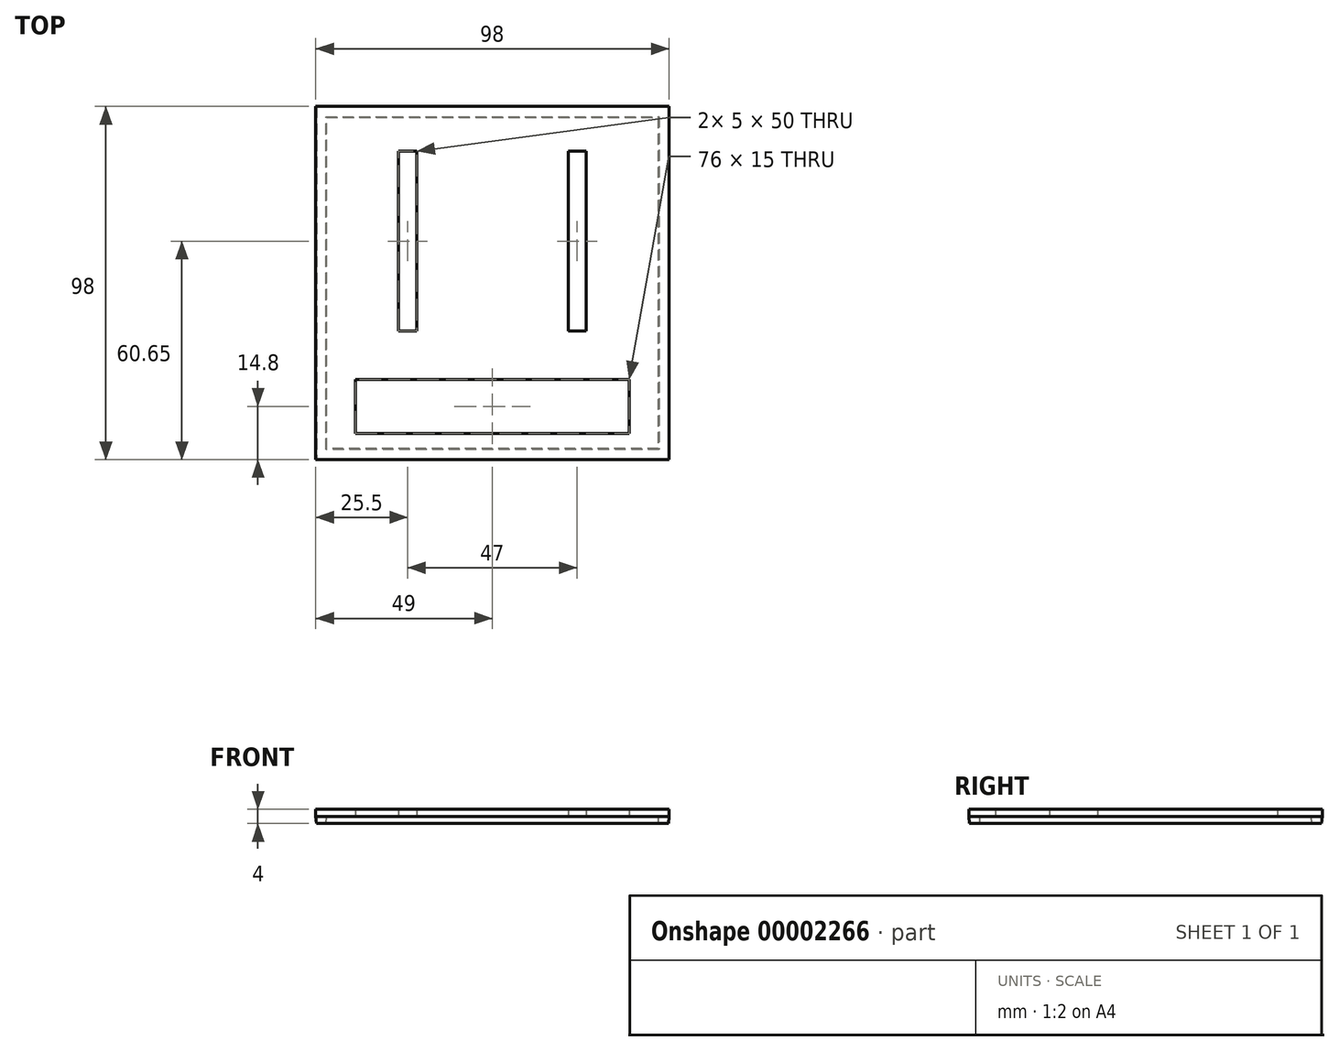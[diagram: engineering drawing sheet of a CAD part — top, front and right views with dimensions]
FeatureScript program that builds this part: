
annotation { "Feature Type Name" : "Feature", "Feature Type Description" : "" }
export const myFeature = defineFeature(function(context is Context, id is Id, definition is map)
    precondition{}
    {
        {
            var Q0;
            Q0=qCreatedBy(makeId("Top.planeOp"),FACE);
            var sketch = newSketch(context, id + "F0", { "sketchPlane" : qUnion([Q0])});
            skLineSegment(sketch, "E0.bottom", {"start": v(46, -46) * mm, "end": v(-46, -46) * mm});
            skLineSegment(sketch, "E0.top", {"start": v(46, 46) * mm, "end": v(-46, 46) * mm});
            skLineSegment(sketch, "E0.left", {"start": v(46, -46) * mm, "end": v(46, 46) * mm});
            skLineSegment(sketch, "E0.right", {"start": v(-46, -46) * mm, "end": v(-46, 46) * mm});
            skPoint(sketch, "E0.middle", {"position": v(0, 0) * mm});
            skLineSegment(sketch, "E1", {"start": v(0, 46) * mm, "end": v(0, -46) * mm, "construction": true});
            skLineSegment(sketch, "E2", {"start": v(0, -41.7) * mm, "end": v(38, -41.7) * mm});
            skLineSegment(sketch, "E3", {"start": v(38, -41.7) * mm, "end": v(38, -26.7) * mm});
            skLineSegment(sketch, "E4", {"start": v(38, -26.7) * mm, "end": v(0, -26.7) * mm});
            skLineSegment(sketch, "E5.bottom", {"start": v(49, 49) * mm, "end": v(-49, 49) * mm});
            skLineSegment(sketch, "E5.top", {"start": v(49, -49) * mm, "end": v(-49, -49) * mm});
            skLineSegment(sketch, "E5.left", {"start": v(49, 49) * mm, "end": v(49, -49) * mm});
            skLineSegment(sketch, "E5.right", {"start": v(-49, 49) * mm, "end": v(-49, -49) * mm});
            skLineSegment(sketch, "E6.bottom", {"start": v(26, -13.35) * mm, "end": v(21, -13.35) * mm});
            skLineSegment(sketch, "E6.top", {"start": v(26, 36.65) * mm, "end": v(21, 36.65) * mm});
            skLineSegment(sketch, "E6.left", {"start": v(26, -13.35) * mm, "end": v(26, 36.65) * mm});
            skLineSegment(sketch, "E6.right", {"start": v(21, -13.35) * mm, "end": v(21, 36.65) * mm});
            skLineSegment(sketch, "E7.MirrorCS", {"start": v(-26, -13.35) * mm, "end": v(-26, 36.65) * mm});
            skLineSegment(sketch, "E8.MirrorCS", {"start": v(-21, -13.35) * mm, "end": v(-21, 36.65) * mm});
            skLineSegment(sketch, "E9.MirrorCS", {"start": v(-26, 36.65) * mm, "end": v(-21, 36.65) * mm});
            skLineSegment(sketch, "E10.MirrorCS", {"start": v(-26, -13.35) * mm, "end": v(-21, -13.35) * mm});
            skLineSegment(sketch, "E11.MirrorCS", {"start": v(-38, -26.7) * mm, "end": v(0, -26.7) * mm});
            skLineSegment(sketch, "E12.MirrorCS", {"start": v(-38, -41.7) * mm, "end": v(-38, -26.7) * mm});
            skLineSegment(sketch, "E13.MirrorCS", {"start": v(0, -41.7) * mm, "end": v(-38, -41.7) * mm});
            skSolve(sketch);
        }
        {
            var Q0;
            Q0=makeQuery(id+"F0.imprint","IMPRINT",FACE,{"disambiguationData":[TD([[makeQuery(id+"F0.imprint","IMPRINT",EDGE,{"derivedFrom":sQuery(id+"F0.wireOp",EDGE,"E0.bottom")}),-1.0]])]});
            var Q1;
            Q1=makeQuery(id+"F0.imprint","IMPRINT",FACE,{"disambiguationData":[TD([[makeQuery(id+"F0.imprint","IMPRINT",EDGE,{"derivedFrom":sQuery(id+"F0.wireOp",EDGE,"E0.bottom")}),1.0]])]});
            extrude(context, id + "F1", {"entities" : qUnion([Q0, Q1]), "depth" : 2 * mm, "offsetDistance" : 25 * mm});
        }
        {
            var Q0;
            Q0=makeQuery(id+"F0.imprint","IMPRINT",FACE,{"disambiguationData":[TD([[makeQuery(id+"F0.imprint","IMPRINT",EDGE,{"derivedFrom":sQuery(id+"F0.wireOp",EDGE,"E0.bottom")}),1.0]])]});
            extrude(context, id + "F2", {"entities" : qUnion([Q0]), "operationType" : NewBodyOperationType.ADD, "oppositeDirection" : true, "depth" : 2 * mm, "offsetDistance" : 25 * mm, "hasDraft" : true, "draftAngle" : 5 * degree, "draftPullDirection" : true});
        }
    });
